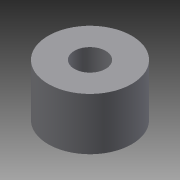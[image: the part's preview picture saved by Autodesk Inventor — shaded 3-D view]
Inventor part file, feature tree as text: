
AUTODESK INVENTOR PART (.ipt)
format: ipt  version: 2013 (Build 170138000, 138)  size: 73,216 bytes
history: native  units: mm
features: extrude x1, sketch x1
ambient origin geometry x8: Origin, YZ Plane, XZ Plane, XY Plane, X Axis, Y Axis, Z Axis, Center Point
bodies: Solid1 (feature_tree)
feature tree (2):
  extrude  "Extrusion1"  Depth=3.0mm
  sketch  "Sketch1"  dims[d0=8.0mm d2=3.0mm d3=5.0mm d4=0.0mm]
